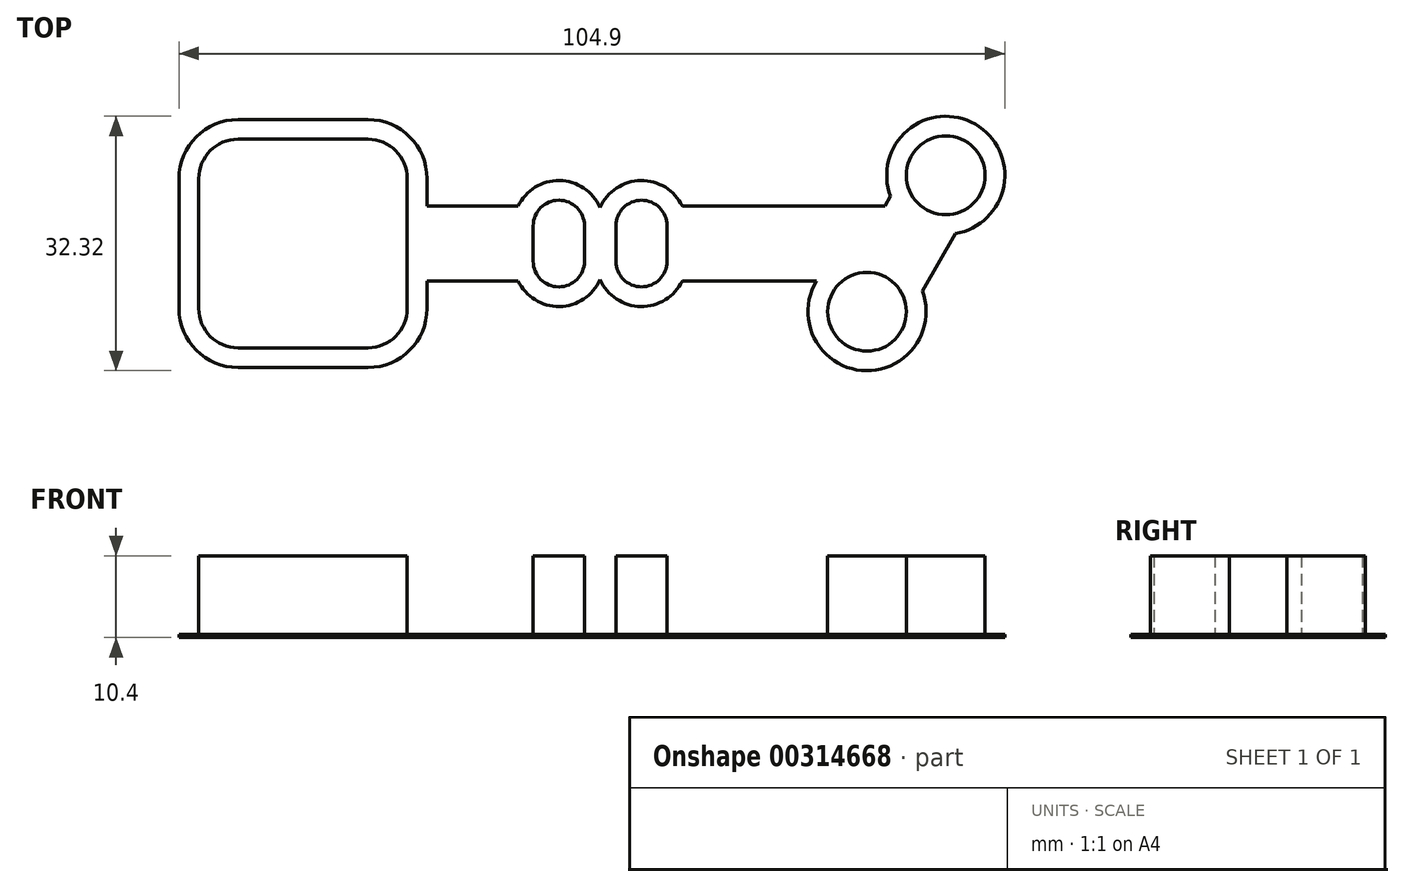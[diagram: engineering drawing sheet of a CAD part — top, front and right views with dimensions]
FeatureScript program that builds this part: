
annotation { "Feature Type Name" : "Feature", "Feature Type Description" : "" }
export const myFeature = defineFeature(function(context is Context, id is Id, definition is map)
    precondition{}
    {
        {
            var Q0;
            Q0=qCreatedBy(makeId("Top.planeOp"),FACE);
            var sketch = newSketch(context, id + "F0", { "sketchPlane" : qUnion([Q0])});
            skLineSegment(sketch, "E0.bottom", {"start": v(-8.25, 13.25) * mm, "end": v(8.25, 13.25) * mm});
            skLineSegment(sketch, "E0.top", {"start": v(-8.25, -13.25) * mm, "end": v(8.25, -13.25) * mm});
            skLineSegment(sketch, "E0.left", {"start": v(-13.25, 8.25) * mm, "end": v(-13.25, -8.25) * mm});
            skLineSegment(sketch, "E0.right", {"start": v(13.25, 8.25) * mm, "end": v(13.25, 8.25) * mm});
            skPoint(sketch, "E0.middle", {"position": v(0, 0) * mm});
            skPoint(sketch, "E1.visualSharp", {"position": v(-13.25, 13.25) * mm});
            skArc(sketch, "E1.filletArc", {"start": v(-8.25, 13.25) * mm, "mid": v(-11.79, 11.79) * mm, "end": v(-13.25, 8.25) * mm});
            skPoint(sketch, "E2.visualSharp", {"position": v(13.25, 13.25) * mm});
            skArc(sketch, "E2.filletArc", {"start": v(13.25, 8.25) * mm, "mid": v(11.79, 11.79) * mm, "end": v(8.25, 13.25) * mm});
            skPoint(sketch, "E3.visualSharp", {"position": v(13.25, -13.25) * mm});
            skArc(sketch, "E3.filletArc", {"start": v(8.25, -13.25) * mm, "mid": v(11.79, -11.79) * mm, "end": v(13.25, -8.25) * mm});
            skPoint(sketch, "E4.visualSharp", {"position": v(-13.25, -13.25) * mm});
            skArc(sketch, "E4.filletArc", {"start": v(-13.25, -8.25) * mm, "mid": v(-11.79, -11.79) * mm, "end": v(-8.25, -13.25) * mm});
            skCircle(sketch, "E5", {"center": v(0, 0) * mm, "radius": 4.5 * mm});
            skLineSegment(sketch, "E6", {"start": v(-75.07, 0) * mm, "end": v(74.58, 0) * mm, "construction": true});
            skPoint(sketch, "E6.startSnap0", {"position": v(-13.25, 0) * mm});
            skPoint(sketch, "E6.endSnap0", {"position": v(-13.25, 0) * mm});
            skLineSegment(sketch, "E7", {"start": v(-4.5, 13.25) * mm, "end": v(-4.5, -13.25) * mm});
            skLineSegment(sketch, "E8", {"start": v(4.5, 13.25) * mm, "end": v(4.5, -13.25) * mm});
            skLineSegment(sketch, "E9", {"start": v(-13.25, 4.5) * mm, "end": v(13.25, 4.5) * mm});
            skLineSegment(sketch, "E10", {"start": v(-13.25, -4.5) * mm, "end": v(13.25, -4.5) * mm});
            skLineSegment(sketch, "E11", {"start": v(13.25, 2.25) * mm, "end": v(29.25, 2.25) * mm});
            skLineSegment(sketch, "E12.bottom", {"start": v(29.25, 2.25) * mm, "end": v(35.75, 2.25) * mm});
            skLineSegment(sketch, "E12.top", {"start": v(29.25, -2.25) * mm, "end": v(35.75, -2.25) * mm});
            skLineSegment(sketch, "E12.left", {"start": v(29.25, 2.25) * mm, "end": v(29.25, -2.25) * mm});
            skLineSegment(sketch, "E12.right", {"start": v(35.75, 2.25) * mm, "end": v(35.75, -2.25) * mm});
            skLineSegment(sketch, "E13", {"start": v(37.75, -24.55) * mm, "end": v(37.75, 21.23) * mm, "construction": true});
            skLineSegment(sketch, "E14.MirrorCS", {"start": v(46.25, 2.25) * mm, "end": v(46.25, -2.25) * mm});
            skLineSegment(sketch, "E15.MirrorCS", {"start": v(46.25, 2.25) * mm, "end": v(39.75, 2.25) * mm});
            skLineSegment(sketch, "E16.MirrorCS", {"start": v(39.75, 2.25) * mm, "end": v(39.75, -2.25) * mm});
            skLineSegment(sketch, "E17.MirrorCS", {"start": v(46.25, -2.25) * mm, "end": v(39.75, -2.25) * mm});
            skLineSegment(sketch, "E18", {"start": v(29.25, -2.25) * mm, "end": v(13.25, -2.25) * mm});
            skLineSegment(sketch, "E19", {"start": v(35.75, 2.25) * mm, "end": v(39.75, 2.25) * mm});
            skLineSegment(sketch, "E20", {"start": v(35.75, -2.25) * mm, "end": v(39.75, -2.25) * mm});
            skArc(sketch, "E21", {"start": v(29.25, 2.25) * mm, "mid": v(32.5, 5.5) * mm, "end": v(35.75, 2.25) * mm});
            skArc(sketch, "E22", {"start": v(29.25, -2.25) * mm, "mid": v(32.5, -5.5) * mm, "end": v(35.75, -2.25) * mm});
            skArc(sketch, "E23.MirrorCS", {"start": v(46.25, -2.25) * mm, "mid": v(43, -5.5) * mm, "end": v(39.75, -2.25) * mm});
            skArc(sketch, "E24.MirrorCS", {"start": v(46.25, 2.25) * mm, "mid": v(43, 5.5) * mm, "end": v(39.75, 2.25) * mm});
            skLineSegment(sketch, "E25", {"start": v(71.65, -8.66) * mm, "end": v(81.65, 8.66) * mm, "construction": true});
            skPoint(sketch, "E26", {"position": v(76.65, 0) * mm});
            skLineSegment(sketch, "E27", {"start": v(77.47, 5.92) * mm, "end": v(77.47, 5.92) * mm});
            skLineSegment(sketch, "E28.MirrorCS", {"start": v(81.36, 3.67) * mm, "end": v(75.83, -5.92) * mm});
            skPoint(sketch, "E29", {"position": v(74.05, 0) * mm});
            skLineSegment(sketch, "E30.MirrorCS", {"start": v(46.25, -2.25) * mm, "end": v(72.75, -2.25) * mm});
            skLineSegment(sketch, "E31", {"start": v(13.25, 4.5) * mm, "end": v(13.25, 4.5) * mm});
            skLineSegment(sketch, "E32", {"start": v(13.25, 8.25) * mm, "end": v(13.25, 4.5) * mm});
            skLineSegment(sketch, "E33", {"start": v(13.25, 4.5) * mm, "end": v(13.25, 2.25) * mm});
            skLineSegment(sketch, "E34", {"start": v(13.25, 2.25) * mm, "end": v(13.25, 2.25) * mm});
            skLineSegment(sketch, "E35", {"start": v(13.25, -2.25) * mm, "end": v(13.25, -2.25) * mm});
            skLineSegment(sketch, "E36", {"start": v(13.25, 2.25) * mm, "end": v(13.25, -2.04) * mm});
            skLineSegment(sketch, "E37", {"start": v(13.25, -4.5) * mm, "end": v(13.25, -8.25) * mm});
            skLineSegment(sketch, "E38", {"start": v(13.25, -2.04) * mm, "end": v(13.25, -2.25) * mm});
            skLineSegment(sketch, "E39", {"start": v(13.25, -2.25) * mm, "end": v(13.25, -4.5) * mm});
            skLineSegment(sketch, "E40", {"start": v(13.25, -4.5) * mm, "end": v(13.25, -4.5) * mm});
            skArc(sketch, "E41", {"start": v(81.36, 3.67) * mm, "mid": v(84.15, 13) * mm, "end": v(77.47, 5.92) * mm});
            skArc(sketch, "E42", {"start": v(77.47, 5.92) * mm, "mid": v(79.13, 4.34) * mm, "end": v(81.31, 3.67) * mm});
            skArc(sketch, "E43", {"start": v(81.31, 3.67) * mm, "mid": v(81.34, 3.67) * mm, "end": v(81.36, 3.67) * mm});
            skArc(sketch, "E44", {"start": v(71.93, -3.67) * mm, "mid": v(71.88, -3.67) * mm, "end": v(71.82, -3.66) * mm});
            skArc(sketch, "E45", {"start": v(75.83, -5.92) * mm, "mid": v(74.13, -4.32) * mm, "end": v(71.88, -3.67) * mm});
            skArc(sketch, "E46", {"start": v(71.88, -3.67) * mm, "mid": v(71.39, -13.65) * mm, "end": v(71.93, -3.67) * mm});
            skLineSegment(sketch, "E47", {"start": v(75.83, -5.92) * mm, "end": v(75.83, -5.92) * mm});
            skLineSegment(sketch, "E48", {"start": v(72.75, -2.25) * mm, "end": v(71.93, -3.67) * mm});
            skArc(sketch, "E49", {"start": v(71.82, -3.66) * mm, "mid": v(69.2, -13.02) * mm, "end": v(75.83, -5.92) * mm});
            skLineSegment(sketch, "E50", {"start": v(46.25, 2.25) * mm, "end": v(75.35, 2.25) * mm});
            skLineSegment(sketch, "E51", {"start": v(75.35, 2.25) * mm, "end": v(72.75, -2.25) * mm});
            skLineSegment(sketch, "E52", {"start": v(77.47, 5.92) * mm, "end": v(75.35, 2.25) * mm});
            skArc(sketch, "E53.0", {"start": v(48.18, -4.75) * mm, "mid": v(42.91, -8) * mm, "end": v(37.75, -4.6) * mm});
            skArc(sketch, "E53.1", {"start": v(27.32, -4.75) * mm, "mid": v(32.59, -8) * mm, "end": v(37.75, -4.6) * mm});
            skLineSegment(sketch, "E53.2", {"start": v(27.32, -4.75) * mm, "end": v(15.75, -4.75) * mm});
            skLineSegment(sketch, "E53.3", {"start": v(15.75, -4.75) * mm, "end": v(15.75, -8.25) * mm});
            skArc(sketch, "E53.4", {"start": v(8.25, -15.75) * mm, "mid": v(13.55, -13.55) * mm, "end": v(15.75, -8.25) * mm});
            skLineSegment(sketch, "E53.5", {"start": v(48.18, -4.75) * mm, "end": v(65.25, -4.75) * mm});
            skLineSegment(sketch, "E53.6", {"start": v(-8.25, -15.75) * mm, "end": v(8.25, -15.75) * mm});
            skArc(sketch, "E53.7", {"start": v(-15.75, -8.25) * mm, "mid": v(-13.55, -13.55) * mm, "end": v(-8.25, -15.75) * mm});
            skLineSegment(sketch, "E53.8", {"start": v(-15.75, 8.25) * mm, "end": v(-15.75, -8.25) * mm});
            skArc(sketch, "E53.9", {"start": v(-8.25, 15.75) * mm, "mid": v(-13.55, 13.55) * mm, "end": v(-15.75, 8.25) * mm});
            skLineSegment(sketch, "E53.10", {"start": v(-8.25, 15.75) * mm, "end": v(8.25, 15.75) * mm});
            skLineSegment(sketch, "E53.11", {"start": v(74.63, 6) * mm, "end": v(73.9, 4.75) * mm});
            skArc(sketch, "E53.12", {"start": v(82.86, 1.26) * mm, "mid": v(85.4, 15.16) * mm, "end": v(74.63, 6) * mm});
            skLineSegment(sketch, "E53.13", {"start": v(82.86, 1.26) * mm, "end": v(78.66, -6) * mm});
            skArc(sketch, "E53.14", {"start": v(65.25, -4.75) * mm, "mid": v(70.95, -16.13) * mm, "end": v(78.66, -6) * mm});
            skLineSegment(sketch, "E53.15", {"start": v(48.18, 4.75) * mm, "end": v(73.9, 4.75) * mm});
            skArc(sketch, "E53.16", {"start": v(48.18, 4.75) * mm, "mid": v(42.91, 8) * mm, "end": v(37.75, 4.6) * mm});
            skArc(sketch, "E53.17", {"start": v(27.32, 4.75) * mm, "mid": v(32.59, 8) * mm, "end": v(37.75, 4.6) * mm});
            skLineSegment(sketch, "E53.18", {"start": v(15.75, 4.75) * mm, "end": v(27.32, 4.75) * mm});
            skLineSegment(sketch, "E53.19", {"start": v(15.75, 8.25) * mm, "end": v(15.75, 4.75) * mm});
            skArc(sketch, "E53.20", {"start": v(15.75, 8.25) * mm, "mid": v(13.55, 13.55) * mm, "end": v(8.25, 15.75) * mm});
            skSolve(sketch);
        }
        {
            var Q0;
            {var subQ0=sQuery(id+"F0.wireOp",EDGE,"E9");var subQ1=sQuery(id+"F0.wireOp",EDGE,"E0.left");var subQ2=makeQuery(id+"F0.imprint","INTERSECT",VERTEX,{"derivedFrom":[subQ1,subQ0]});Q0=makeQuery(id+"F0.imprint","IMPRINT",FACE,{"disambiguationData":[TD([[makeQuery(id+"F0.imprint","IMPRINT",EDGE,{"disambiguationData":[TD([[subQ2,-1.0]])],"derivedFrom":subQ1}),1.0]])]});}
            var Q1;
            {var subQ0=sQuery(id+"F0.wireOp",EDGE,"E33");Q1=makeQuery(id+"F0.imprint","IMPRINT",FACE,{"disambiguationData":[TD([[makeQuery(id+"F0.imprint","IMPRINT",EDGE,{"derivedFrom":subQ0}),-1.0]])]});}
            var Q2;
            {var subQ0=sQuery(id+"F0.wireOp",EDGE,"E9");var subQ1=sQuery(id+"F0.wireOp",EDGE,"E5");var subQ2=makeQuery(id+"F0.imprint","INTERSECT",VERTEX,{"derivedFrom":[subQ1,subQ0]});Q2=makeQuery(id+"F0.imprint","IMPRINT",FACE,{"disambiguationData":[TD([[makeQuery(id+"F0.imprint","IMPRINT",EDGE,{"disambiguationData":[TD([[subQ2,1.0]])],"derivedFrom":subQ1}),-1.0]])]});}
            var Q3;
            {var subQ0=sQuery(id+"F0.wireOp",EDGE,"E5");var subQ1=makeQuery(id+"F0.imprint","INTERSECT",VERTEX,{"derivedFrom":[subQ0,sQuery(id+"F0.wireOp",EDGE,"E9")]});Q3=makeQuery(id+"F0.imprint","IMPRINT",FACE,{"disambiguationData":[TD([[makeQuery(id+"F0.imprint","IMPRINT",EDGE,{"disambiguationData":[TD([[subQ1,1.0]])],"derivedFrom":subQ0}),1.0]])]});}
            var Q4;
            {var subQ6=sQuery(id+"F0.wireOp",EDGE,"E3.filletArc");Q4=makeQuery(id+"F0.imprint","IMPRINT",FACE,{"disambiguationData":[TD([[makeQuery(id+"F0.imprint","IMPRINT",EDGE,{"derivedFrom":subQ6}),1.0]])]});}
            var Q5;
            {var subQ5=sQuery(id+"F0.wireOp",EDGE,"E1.filletArc");Q5=makeQuery(id+"F0.imprint","IMPRINT",FACE,{"disambiguationData":[TD([[makeQuery(id+"F0.imprint","IMPRINT",EDGE,{"derivedFrom":subQ5}),1.0]])]});}
            var Q6;
            {var subQ6=sQuery(id+"F0.wireOp",EDGE,"E2.filletArc");Q6=makeQuery(id+"F0.imprint","IMPRINT",FACE,{"disambiguationData":[TD([[makeQuery(id+"F0.imprint","IMPRINT",EDGE,{"derivedFrom":subQ6}),1.0]])]});}
            var Q7;
            {var subQ0=sQuery(id+"F0.wireOp",EDGE,"E9");var subQ1=sQuery(id+"F0.wireOp",EDGE,"E5");var subQ2=makeQuery(id+"F0.imprint","INTERSECT",VERTEX,{"derivedFrom":[subQ1,subQ0]});Q7=makeQuery(id+"F0.imprint","IMPRINT",FACE,{"disambiguationData":[TD([[makeQuery(id+"F0.imprint","IMPRINT",EDGE,{"disambiguationData":[TD([[subQ2,-1.0]])],"derivedFrom":subQ1}),-1.0]])]});}
            var Q8;
            {var subQ0=sQuery(id+"F0.wireOp",EDGE,"E7");var subQ1=sQuery(id+"F0.wireOp",EDGE,"E5");var subQ2=makeQuery(id+"F0.imprint","INTERSECT",VERTEX,{"derivedFrom":[subQ1,subQ0]});Q8=makeQuery(id+"F0.imprint","IMPRINT",FACE,{"disambiguationData":[TD([[makeQuery(id+"F0.imprint","IMPRINT",EDGE,{"disambiguationData":[TD([[subQ2,-1.0]])],"derivedFrom":subQ1}),-1.0]])]});}
            var Q9;
            {var subQ5=sQuery(id+"F0.wireOp",EDGE,"E4.filletArc");Q9=makeQuery(id+"F0.imprint","IMPRINT",FACE,{"disambiguationData":[TD([[makeQuery(id+"F0.imprint","IMPRINT",EDGE,{"derivedFrom":subQ5}),1.0]])]});}
            var Q10;
            {var subQ2=sQuery(id+"F0.wireOp",EDGE,"E7");var subQ4=sQuery(id+"F0.wireOp",EDGE,"E0.top");var subQ5=makeQuery(id+"F0.imprint","INTERSECT",VERTEX,{"derivedFrom":[subQ4,subQ2]});Q10=makeQuery(id+"F0.imprint","IMPRINT",FACE,{"disambiguationData":[TD([[makeQuery(id+"F0.imprint","IMPRINT",EDGE,{"disambiguationData":[TD([[subQ5,-1.0]])],"derivedFrom":subQ4}),1.0]])]});}
            var Q11;
            Q11=makeQuery(id+"F0.imprint","IMPRINT",FACE,{"disambiguationData":[TD([[makeQuery(id+"F0.imprint","IMPRINT",EDGE,{"derivedFrom":sQuery(id+"F0.wireOp",EDGE,"E12.right")}),1.0]])]});
            var Q12;
            {var subQ0=sQuery(id+"F0.wireOp",EDGE,"E45");Q12=makeQuery(id+"F0.imprint","IMPRINT",FACE,{"disambiguationData":[TD([[makeQuery(id+"F0.imprint","IMPRINT",EDGE,{"derivedFrom":subQ0}),1.0]])]});}
            var Q13;
            Q13=makeQuery(id+"F0.imprint","IMPRINT",FACE,{"disambiguationData":[TD([[makeQuery(id+"F0.imprint","IMPRINT",EDGE,{"derivedFrom":sQuery(id+"F0.wireOp",EDGE,"E12.bottom")}),-1.0]])]});
            var Q14;
            {var subQ0=sQuery(id+"F0.wireOp",EDGE,"E8");var subQ1=sQuery(id+"F0.wireOp",EDGE,"E5");var subQ2=makeQuery(id+"F0.imprint","INTERSECT",VERTEX,{"derivedFrom":[subQ1,subQ0]});Q14=makeQuery(id+"F0.imprint","IMPRINT",FACE,{"disambiguationData":[TD([[makeQuery(id+"F0.imprint","IMPRINT",EDGE,{"disambiguationData":[TD([[subQ2,1.0]])],"derivedFrom":subQ1}),-1.0]])]});}
            var Q15;
            Q15=makeQuery(id+"F0.imprint","IMPRINT",FACE,{"disambiguationData":[TD([[makeQuery(id+"F0.imprint","IMPRINT",EDGE,{"derivedFrom":sQuery(id+"F0.wireOp",EDGE,"E14.MirrorCS")}),1.0]])]});
            var Q16;
            Q16=makeQuery(id+"F0.imprint","IMPRINT",FACE,{"disambiguationData":[TD([[makeQuery(id+"F0.imprint","IMPRINT",EDGE,{"derivedFrom":sQuery(id+"F0.wireOp",EDGE,"E11")}),-1.0]])]});
            var Q17;
            Q17=makeQuery(id+"F0.imprint","IMPRINT",FACE,{"disambiguationData":[TD([[makeQuery(id+"F0.imprint","IMPRINT",EDGE,{"derivedFrom":sQuery(id+"F0.wireOp",EDGE,"E41")}),1.0]])]});
            var Q18;
            Q18=makeQuery(id+"F0.imprint","IMPRINT",FACE,{"disambiguationData":[TD([[makeQuery(id+"F0.imprint","IMPRINT",EDGE,{"derivedFrom":sQuery(id+"F0.wireOp",EDGE,"E17.MirrorCS")}),1.0]])]});
            var Q19;
            Q19=makeQuery(id+"F0.imprint","IMPRINT",FACE,{"disambiguationData":[TD([[makeQuery(id+"F0.imprint","IMPRINT",EDGE,{"derivedFrom":sQuery(id+"F0.wireOp",EDGE,"E15.MirrorCS")}),-1.0]])]});
            var Q20;
            Q20=makeQuery(id+"F0.imprint","IMPRINT",FACE,{"disambiguationData":[TD([[makeQuery(id+"F0.imprint","IMPRINT",EDGE,{"derivedFrom":sQuery(id+"F0.wireOp",EDGE,"E12.top")}),-1.0]])]});
            var Q21;
            Q21=makeQuery(id+"F0.imprint","IMPRINT",FACE,{"disambiguationData":[TD([[makeQuery(id+"F0.imprint","IMPRINT",EDGE,{"derivedFrom":sQuery(id+"F0.wireOp",EDGE,"E12.bottom")}),1.0]])]});
            var Q22;
            {var subQ3=sQuery(id+"F0.wireOp",EDGE,"E1.filletArc");Q22=makeQuery(id+"F0.imprint","IMPRINT",FACE,{"disambiguationData":[TD([[makeQuery(id+"F0.imprint","IMPRINT",EDGE,{"derivedFrom":subQ3}),-1.0]])]});}
            var Q23;
            {var subQ0=sQuery(id+"F0.wireOp",EDGE,"E7");var subQ1=sQuery(id+"F0.wireOp",EDGE,"E0.bottom");var subQ2=makeQuery(id+"F0.imprint","INTERSECT",VERTEX,{"derivedFrom":[subQ1,subQ0]});Q23=makeQuery(id+"F0.imprint","IMPRINT",FACE,{"disambiguationData":[TD([[makeQuery(id+"F0.imprint","IMPRINT",EDGE,{"disambiguationData":[TD([[subQ2,-1.0]])],"derivedFrom":subQ1}),-1.0]])]});}
            var Q24;
            {var subQ1=sQuery(id+"F0.wireOp",EDGE,"E28.MirrorCS");Q24=makeQuery(id+"F0.imprint","IMPRINT",FACE,{"disambiguationData":[TD([[makeQuery(id+"F0.imprint","IMPRINT",EDGE,{"derivedFrom":subQ1}),-1.0]])]});}
            var Q25;
            Q25=makeQuery(id+"F0.imprint","IMPRINT",FACE,{"disambiguationData":[TD([[makeQuery(id+"F0.imprint","IMPRINT",EDGE,{"derivedFrom":sQuery(id+"F0.wireOp",EDGE,"E14.MirrorCS")}),-1.0]])]});
            extrude(context, id + "F1", {"entities" : qUnion([Q0, Q1, Q2, Q3, Q4, Q5, Q6, Q7, Q8, Q9, Q10, Q11, Q12, Q13, Q14, Q15, Q16, Q17, Q18, Q19, Q20, Q21, Q22, Q23, Q24, Q25]), "depth" : 0.4 * mm});
        }
        {
            var Q0;
            Q0=makeQuery(id+"F1.opExtrude","CAP_FACE",FACE,{"disambiguationData":[OSD([sQuery(id+"F0.wireOp",EDGE,"E53.0"),sQuery(id+"F0.wireOp",EDGE,"E53.1"),sQuery(id+"F0.wireOp",EDGE,"E53.2"),sQuery(id+"F0.wireOp",EDGE,"E53.3"),sQuery(id+"F0.wireOp",EDGE,"E53.4"),sQuery(id+"F0.wireOp",EDGE,"E53.5"),sQuery(id+"F0.wireOp",EDGE,"E53.6"),sQuery(id+"F0.wireOp",EDGE,"E53.7"),sQuery(id+"F0.wireOp",EDGE,"E53.8"),sQuery(id+"F0.wireOp",EDGE,"E53.9"),sQuery(id+"F0.wireOp",EDGE,"E53.10"),sQuery(id+"F0.wireOp",EDGE,"E53.11"),sQuery(id+"F0.wireOp",EDGE,"E53.12"),sQuery(id+"F0.wireOp",EDGE,"E53.13"),sQuery(id+"F0.wireOp",EDGE,"E53.14"),sQuery(id+"F0.wireOp",EDGE,"E53.15"),sQuery(id+"F0.wireOp",EDGE,"E53.16"),sQuery(id+"F0.wireOp",EDGE,"E53.17"),sQuery(id+"F0.wireOp",EDGE,"E53.18"),sQuery(id+"F0.wireOp",EDGE,"E53.19"),sQuery(id+"F0.wireOp",EDGE,"E53.20")])],"isStart":false});
            var sketch = newSketch(context, id + "F2", { "sketchPlane" : qUnion([Q0])});
            skLineSegment(sketch, "E54.0", {"start": v(-8.25, 13.25) * mm, "end": v(8.25, 13.25) * mm});
            skLineSegment(sketch, "E54.1", {"start": v(-8.25, -13.25) * mm, "end": v(8.25, -13.25) * mm});
            skLineSegment(sketch, "E54.2", {"start": v(-13.25, 8.25) * mm, "end": v(-13.25, -8.25) * mm});
            skPoint(sketch, "E54.3", {"position": v(13.25, 8.25) * mm});
            skPoint(sketch, "E54.4", {"position": v(0, 0) * mm});
            skPoint(sketch, "E54.5", {"position": v(-13.25, 13.25) * mm});
            skArc(sketch, "E54.6", {"start": v(-8.25, 13.25) * mm, "mid": v(-11.79, 11.79) * mm, "end": v(-13.25, 8.25) * mm});
            skPoint(sketch, "E54.7", {"position": v(13.25, 13.25) * mm});
            skArc(sketch, "E54.8", {"start": v(13.25, 8.25) * mm, "mid": v(11.79, 11.79) * mm, "end": v(8.25, 13.25) * mm});
            skPoint(sketch, "E54.9", {"position": v(13.25, -13.25) * mm});
            skArc(sketch, "E54.10", {"start": v(8.25, -13.25) * mm, "mid": v(11.79, -11.79) * mm, "end": v(13.25, -8.25) * mm});
            skPoint(sketch, "E54.11", {"position": v(-13.25, -13.25) * mm});
            skArc(sketch, "E54.12", {"start": v(-13.25, -8.25) * mm, "mid": v(-11.79, -11.79) * mm, "end": v(-8.25, -13.25) * mm});
            skCircle(sketch, "E54.13", {"center": v(0, 0) * mm, "radius": 4.5 * mm});
            skPoint(sketch, "E54.15", {"position": v(-13.25, 0) * mm});
            skPoint(sketch, "E54.16", {"position": v(-13.25, 0) * mm});
            skLineSegment(sketch, "E54.17", {"start": v(-4.5, 13.25) * mm, "end": v(-4.5, -13.25) * mm});
            skLineSegment(sketch, "E54.18", {"start": v(4.5, 13.25) * mm, "end": v(4.5, -13.25) * mm});
            skLineSegment(sketch, "E54.19", {"start": v(-13.25, 4.5) * mm, "end": v(13.25, 4.5) * mm});
            skLineSegment(sketch, "E54.20", {"start": v(-13.25, -4.5) * mm, "end": v(13.25, -4.5) * mm});
            skLineSegment(sketch, "E54.21", {"start": v(13.25, 2.25) * mm, "end": v(29.25, 2.25) * mm});
            skLineSegment(sketch, "E54.22", {"start": v(29.25, 2.25) * mm, "end": v(35.75, 2.25) * mm});
            skLineSegment(sketch, "E54.23", {"start": v(29.25, -2.25) * mm, "end": v(35.75, -2.25) * mm});
            skLineSegment(sketch, "E54.24", {"start": v(29.25, 2.25) * mm, "end": v(29.25, -2.25) * mm});
            skLineSegment(sketch, "E54.25", {"start": v(35.75, 2.25) * mm, "end": v(35.75, -2.25) * mm});
            skLineSegment(sketch, "E54.27", {"start": v(46.25, 2.25) * mm, "end": v(46.25, -2.25) * mm});
            skLineSegment(sketch, "E54.28", {"start": v(46.25, 2.25) * mm, "end": v(39.75, 2.25) * mm});
            skLineSegment(sketch, "E54.29", {"start": v(39.75, 2.25) * mm, "end": v(39.75, -2.25) * mm});
            skLineSegment(sketch, "E54.30", {"start": v(46.25, -2.25) * mm, "end": v(39.75, -2.25) * mm});
            skLineSegment(sketch, "E54.31", {"start": v(29.25, -2.25) * mm, "end": v(13.25, -2.25) * mm});
            skLineSegment(sketch, "E54.32", {"start": v(35.75, 2.25) * mm, "end": v(39.75, 2.25) * mm});
            skLineSegment(sketch, "E54.33", {"start": v(35.75, -2.25) * mm, "end": v(39.75, -2.25) * mm});
            skArc(sketch, "E54.34", {"start": v(29.25, 2.25) * mm, "mid": v(32.5, 5.5) * mm, "end": v(35.75, 2.25) * mm});
            skArc(sketch, "E54.35", {"start": v(29.25, -2.25) * mm, "mid": v(32.5, -5.5) * mm, "end": v(35.75, -2.25) * mm});
            skArc(sketch, "E54.36", {"start": v(46.25, -2.25) * mm, "mid": v(43, -5.5) * mm, "end": v(39.75, -2.25) * mm});
            skArc(sketch, "E54.37", {"start": v(46.25, 2.25) * mm, "mid": v(43, 5.5) * mm, "end": v(39.75, 2.25) * mm});
            skLineSegment(sketch, "E54.38", {"start": v(71.65, -8.66) * mm, "end": v(81.65, 8.66) * mm});
            skPoint(sketch, "E54.39", {"position": v(76.65, 0) * mm});
            skPoint(sketch, "E54.40", {"position": v(77.47, 5.92) * mm});
            skLineSegment(sketch, "E54.41", {"start": v(81.36, 3.67) * mm, "end": v(75.83, -5.92) * mm});
            skPoint(sketch, "E54.42", {"position": v(74.05, 0) * mm});
            skLineSegment(sketch, "E54.43", {"start": v(46.25, -2.25) * mm, "end": v(72.75, -2.25) * mm});
            skPoint(sketch, "E54.44", {"position": v(13.25, 4.5) * mm});
            skLineSegment(sketch, "E54.45", {"start": v(13.25, 8.25) * mm, "end": v(13.25, 4.5) * mm});
            skLineSegment(sketch, "E54.46", {"start": v(13.25, 4.5) * mm, "end": v(13.25, 2.25) * mm});
            skPoint(sketch, "E54.47", {"position": v(13.25, 2.25) * mm});
            skPoint(sketch, "E54.48", {"position": v(13.25, -2.25) * mm});
            skLineSegment(sketch, "E54.49", {"start": v(13.25, 2.25) * mm, "end": v(13.25, -2.04) * mm});
            skLineSegment(sketch, "E54.50", {"start": v(13.25, -4.5) * mm, "end": v(13.25, -8.25) * mm});
            skLineSegment(sketch, "E54.51", {"start": v(13.25, -2.04) * mm, "end": v(13.25, -2.25) * mm});
            skLineSegment(sketch, "E54.52", {"start": v(13.25, -2.25) * mm, "end": v(13.25, -4.5) * mm});
            skPoint(sketch, "E54.53", {"position": v(13.25, -4.5) * mm});
            skArc(sketch, "E54.54", {"start": v(81.36, 3.67) * mm, "mid": v(84.15, 13) * mm, "end": v(77.47, 5.92) * mm});
            skArc(sketch, "E54.55", {"start": v(77.47, 5.92) * mm, "mid": v(79.13, 4.34) * mm, "end": v(81.31, 3.67) * mm});
            skPoint(sketch, "E54.56", {"position": v(77.47, 5.92) * mm});
            skArc(sketch, "E54.57", {"start": v(81.31, 3.67) * mm, "mid": v(81.34, 3.67) * mm, "end": v(81.36, 3.67) * mm});
            skArc(sketch, "E54.58", {"start": v(71.93, -3.67) * mm, "mid": v(71.88, -3.67) * mm, "end": v(71.82, -3.66) * mm});
            skArc(sketch, "E54.59", {"start": v(75.83, -5.92) * mm, "mid": v(74.13, -4.32) * mm, "end": v(71.88, -3.67) * mm});
            skArc(sketch, "E54.60", {"start": v(71.88, -3.67) * mm, "mid": v(71.39, -13.65) * mm, "end": v(71.93, -3.67) * mm});
            skPoint(sketch, "E54.61", {"position": v(75.83, -5.92) * mm});
            skLineSegment(sketch, "E54.62", {"start": v(72.75, -2.25) * mm, "end": v(71.93, -3.67) * mm});
            skArc(sketch, "E54.63", {"start": v(71.82, -3.66) * mm, "mid": v(69.2, -13.02) * mm, "end": v(75.83, -5.92) * mm});
            skLineSegment(sketch, "E54.64", {"start": v(46.25, 2.25) * mm, "end": v(75.35, 2.25) * mm});
            skLineSegment(sketch, "E54.65", {"start": v(75.35, 2.25) * mm, "end": v(72.75, -2.25) * mm});
            skLineSegment(sketch, "E54.66", {"start": v(77.47, 5.92) * mm, "end": v(75.35, 2.25) * mm});
            skArc(sketch, "E54.67", {"start": v(48.18, -4.75) * mm, "mid": v(42.91, -8) * mm, "end": v(37.75, -4.6) * mm});
            skArc(sketch, "E54.68", {"start": v(27.32, -4.75) * mm, "mid": v(32.59, -8) * mm, "end": v(37.75, -4.6) * mm});
            skLineSegment(sketch, "E54.69", {"start": v(27.32, -4.75) * mm, "end": v(15.75, -4.75) * mm});
            skLineSegment(sketch, "E54.70", {"start": v(15.75, -4.75) * mm, "end": v(15.75, -8.25) * mm});
            skArc(sketch, "E54.71", {"start": v(8.25, -15.75) * mm, "mid": v(13.55, -13.55) * mm, "end": v(15.75, -8.25) * mm});
            skLineSegment(sketch, "E54.72", {"start": v(48.18, -4.75) * mm, "end": v(65.25, -4.75) * mm});
            skLineSegment(sketch, "E54.73", {"start": v(-8.25, -15.75) * mm, "end": v(8.25, -15.75) * mm});
            skArc(sketch, "E54.74", {"start": v(-15.75, -8.25) * mm, "mid": v(-13.55, -13.55) * mm, "end": v(-8.25, -15.75) * mm});
            skLineSegment(sketch, "E54.75", {"start": v(-15.75, 8.25) * mm, "end": v(-15.75, -8.25) * mm});
            skArc(sketch, "E54.76", {"start": v(-8.25, 15.75) * mm, "mid": v(-13.55, 13.55) * mm, "end": v(-15.75, 8.25) * mm});
            skLineSegment(sketch, "E54.77", {"start": v(-8.25, 15.75) * mm, "end": v(8.25, 15.75) * mm});
            skLineSegment(sketch, "E54.78", {"start": v(74.63, 6) * mm, "end": v(73.9, 4.75) * mm});
            skArc(sketch, "E54.79", {"start": v(82.86, 1.26) * mm, "mid": v(85.4, 15.16) * mm, "end": v(74.63, 6) * mm});
            skLineSegment(sketch, "E54.80", {"start": v(82.86, 1.26) * mm, "end": v(78.66, -6) * mm});
            skArc(sketch, "E54.81", {"start": v(65.25, -4.75) * mm, "mid": v(70.95, -16.13) * mm, "end": v(78.66, -6) * mm});
            skLineSegment(sketch, "E54.82", {"start": v(48.18, 4.75) * mm, "end": v(73.9, 4.75) * mm});
            skArc(sketch, "E54.83", {"start": v(48.18, 4.75) * mm, "mid": v(42.91, 8) * mm, "end": v(37.75, 4.6) * mm});
            skArc(sketch, "E54.84", {"start": v(27.32, 4.75) * mm, "mid": v(32.59, 8) * mm, "end": v(37.75, 4.6) * mm});
            skLineSegment(sketch, "E54.85", {"start": v(15.75, 4.75) * mm, "end": v(27.32, 4.75) * mm});
            skLineSegment(sketch, "E54.86", {"start": v(15.75, 8.25) * mm, "end": v(15.75, 4.75) * mm});
            skArc(sketch, "E54.87", {"start": v(15.75, 8.25) * mm, "mid": v(13.55, 13.55) * mm, "end": v(8.25, 15.75) * mm});
            skSolve(sketch);
        }
        {
            var Q0;
            {var subQ5=sQuery(id+"F2.wireOp",EDGE,"E54.6");Q0=makeQuery(id+"F2.imprint","IMPRINT",FACE,{"disambiguationData":[TD([[makeQuery(id+"F2.imprint","IMPRINT",EDGE,{"derivedFrom":subQ5}),1.0]])]});}
            var Q1;
            {var subQ0=sQuery(id+"F2.wireOp",EDGE,"E54.17");var subQ1=sQuery(id+"F2.wireOp",EDGE,"E54.0");var subQ2=makeQuery(id+"F2.imprint","INTERSECT",VERTEX,{"derivedFrom":[subQ1,subQ0]});Q1=makeQuery(id+"F2.imprint","IMPRINT",FACE,{"disambiguationData":[TD([[makeQuery(id+"F2.imprint","IMPRINT",EDGE,{"disambiguationData":[TD([[subQ2,-1.0]])],"derivedFrom":subQ1}),-1.0]])]});}
            var Q2;
            {var subQ6=sQuery(id+"F2.wireOp",EDGE,"E54.8");Q2=makeQuery(id+"F2.imprint","IMPRINT",FACE,{"disambiguationData":[TD([[makeQuery(id+"F2.imprint","IMPRINT",EDGE,{"derivedFrom":subQ6}),1.0]])]});}
            var Q3;
            {var subQ0=sQuery(id+"F2.wireOp",EDGE,"E54.46");Q3=makeQuery(id+"F2.imprint","IMPRINT",FACE,{"disambiguationData":[TD([[makeQuery(id+"F2.imprint","IMPRINT",EDGE,{"derivedFrom":subQ0}),-1.0]])]});}
            var Q4;
            {var subQ6=sQuery(id+"F2.wireOp",EDGE,"E54.10");Q4=makeQuery(id+"F2.imprint","IMPRINT",FACE,{"disambiguationData":[TD([[makeQuery(id+"F2.imprint","IMPRINT",EDGE,{"derivedFrom":subQ6}),1.0]])]});}
            var Q5;
            {var subQ2=sQuery(id+"F2.wireOp",EDGE,"E54.17");var subQ4=sQuery(id+"F2.wireOp",EDGE,"E54.1");var subQ5=makeQuery(id+"F2.imprint","INTERSECT",VERTEX,{"derivedFrom":[subQ4,subQ2]});Q5=makeQuery(id+"F2.imprint","IMPRINT",FACE,{"disambiguationData":[TD([[makeQuery(id+"F2.imprint","IMPRINT",EDGE,{"disambiguationData":[TD([[subQ5,-1.0]])],"derivedFrom":subQ4}),1.0]])]});}
            var Q6;
            {var subQ5=sQuery(id+"F2.wireOp",EDGE,"E54.12");Q6=makeQuery(id+"F2.imprint","IMPRINT",FACE,{"disambiguationData":[TD([[makeQuery(id+"F2.imprint","IMPRINT",EDGE,{"derivedFrom":subQ5}),1.0]])]});}
            var Q7;
            {var subQ0=sQuery(id+"F2.wireOp",EDGE,"E54.19");var subQ1=sQuery(id+"F2.wireOp",EDGE,"E54.2");var subQ2=makeQuery(id+"F2.imprint","INTERSECT",VERTEX,{"derivedFrom":[subQ1,subQ0]});Q7=makeQuery(id+"F2.imprint","IMPRINT",FACE,{"disambiguationData":[TD([[makeQuery(id+"F2.imprint","IMPRINT",EDGE,{"disambiguationData":[TD([[subQ2,-1.0]])],"derivedFrom":subQ1}),1.0]])]});}
            var Q8;
            {var subQ0=sQuery(id+"F2.wireOp",EDGE,"E54.13");var subQ1=makeQuery(id+"F2.imprint","INTERSECT",VERTEX,{"derivedFrom":[subQ0,sQuery(id+"F2.wireOp",EDGE,"E54.19")]});Q8=makeQuery(id+"F2.imprint","IMPRINT",FACE,{"disambiguationData":[TD([[makeQuery(id+"F2.imprint","IMPRINT",EDGE,{"disambiguationData":[TD([[subQ1,1.0]])],"derivedFrom":subQ0}),1.0]])]});}
            var Q9;
            {var subQ0=sQuery(id+"F2.wireOp",EDGE,"E54.18");var subQ1=sQuery(id+"F2.wireOp",EDGE,"E54.13");var subQ2=makeQuery(id+"F2.imprint","INTERSECT",VERTEX,{"derivedFrom":[subQ1,subQ0]});Q9=makeQuery(id+"F2.imprint","IMPRINT",FACE,{"disambiguationData":[TD([[makeQuery(id+"F2.imprint","IMPRINT",EDGE,{"disambiguationData":[TD([[subQ2,1.0]])],"derivedFrom":subQ1}),-1.0]])]});}
            var Q10;
            {var subQ0=sQuery(id+"F2.wireOp",EDGE,"E54.19");var subQ1=sQuery(id+"F2.wireOp",EDGE,"E54.13");var subQ2=makeQuery(id+"F2.imprint","INTERSECT",VERTEX,{"derivedFrom":[subQ1,subQ0]});Q10=makeQuery(id+"F2.imprint","IMPRINT",FACE,{"disambiguationData":[TD([[makeQuery(id+"F2.imprint","IMPRINT",EDGE,{"disambiguationData":[TD([[subQ2,1.0]])],"derivedFrom":subQ1}),-1.0]])]});}
            var Q11;
            {var subQ0=sQuery(id+"F2.wireOp",EDGE,"E54.19");var subQ1=sQuery(id+"F2.wireOp",EDGE,"E54.13");var subQ2=makeQuery(id+"F2.imprint","INTERSECT",VERTEX,{"derivedFrom":[subQ1,subQ0]});Q11=makeQuery(id+"F2.imprint","IMPRINT",FACE,{"disambiguationData":[TD([[makeQuery(id+"F2.imprint","IMPRINT",EDGE,{"disambiguationData":[TD([[subQ2,-1.0]])],"derivedFrom":subQ1}),-1.0]])]});}
            var Q12;
            {var subQ0=sQuery(id+"F2.wireOp",EDGE,"E54.17");var subQ1=sQuery(id+"F2.wireOp",EDGE,"E54.13");var subQ2=makeQuery(id+"F2.imprint","INTERSECT",VERTEX,{"derivedFrom":[subQ1,subQ0]});Q12=makeQuery(id+"F2.imprint","IMPRINT",FACE,{"disambiguationData":[TD([[makeQuery(id+"F2.imprint","IMPRINT",EDGE,{"disambiguationData":[TD([[subQ2,-1.0]])],"derivedFrom":subQ1}),-1.0]])]});}
            var Q13;
            Q13=makeQuery(id+"F2.imprint","IMPRINT",FACE,{"disambiguationData":[TD([[makeQuery(id+"F2.imprint","IMPRINT",EDGE,{"derivedFrom":sQuery(id+"F2.wireOp",EDGE,"E54.22")}),1.0]])]});
            var Q14;
            Q14=makeQuery(id+"F2.imprint","IMPRINT",FACE,{"disambiguationData":[TD([[makeQuery(id+"F2.imprint","IMPRINT",EDGE,{"derivedFrom":sQuery(id+"F2.wireOp",EDGE,"E54.22")}),-1.0]])]});
            var Q15;
            Q15=makeQuery(id+"F2.imprint","IMPRINT",FACE,{"disambiguationData":[TD([[makeQuery(id+"F2.imprint","IMPRINT",EDGE,{"derivedFrom":sQuery(id+"F2.wireOp",EDGE,"E54.23")}),-1.0]])]});
            var Q16;
            Q16=makeQuery(id+"F2.imprint","IMPRINT",FACE,{"disambiguationData":[TD([[makeQuery(id+"F2.imprint","IMPRINT",EDGE,{"derivedFrom":sQuery(id+"F2.wireOp",EDGE,"E54.30")}),1.0]])]});
            var Q17;
            Q17=makeQuery(id+"F2.imprint","IMPRINT",FACE,{"disambiguationData":[TD([[makeQuery(id+"F2.imprint","IMPRINT",EDGE,{"derivedFrom":sQuery(id+"F2.wireOp",EDGE,"E54.27")}),-1.0]])]});
            var Q18;
            Q18=makeQuery(id+"F2.imprint","IMPRINT",FACE,{"disambiguationData":[TD([[makeQuery(id+"F2.imprint","IMPRINT",EDGE,{"derivedFrom":sQuery(id+"F2.wireOp",EDGE,"E54.28")}),-1.0]])]});
            var Q19;
            {var subQ0=sQuery(id+"F2.wireOp",EDGE,"E54.54");Q19=makeQuery(id+"F2.imprint","IMPRINT",FACE,{"disambiguationData":[TD([[makeQuery(id+"F2.imprint","IMPRINT",EDGE,{"derivedFrom":subQ0}),1.0]])]});}
            var Q20;
            {var subQ1=sQuery(id+"F2.wireOp",EDGE,"E54.59");Q20=makeQuery(id+"F2.imprint","IMPRINT",FACE,{"disambiguationData":[TD([[makeQuery(id+"F2.imprint","IMPRINT",EDGE,{"derivedFrom":subQ1}),1.0]])]});}
            extrude(context, id + "F3", {"entities" : qUnion([Q0, Q1, Q2, Q3, Q4, Q5, Q6, Q7, Q8, Q9, Q10, Q11, Q12, Q13, Q14, Q15, Q16, Q17, Q18, Q19, Q20]), "operationType" : NewBodyOperationType.ADD, "depth" : 10 * mm});
        }
    });
